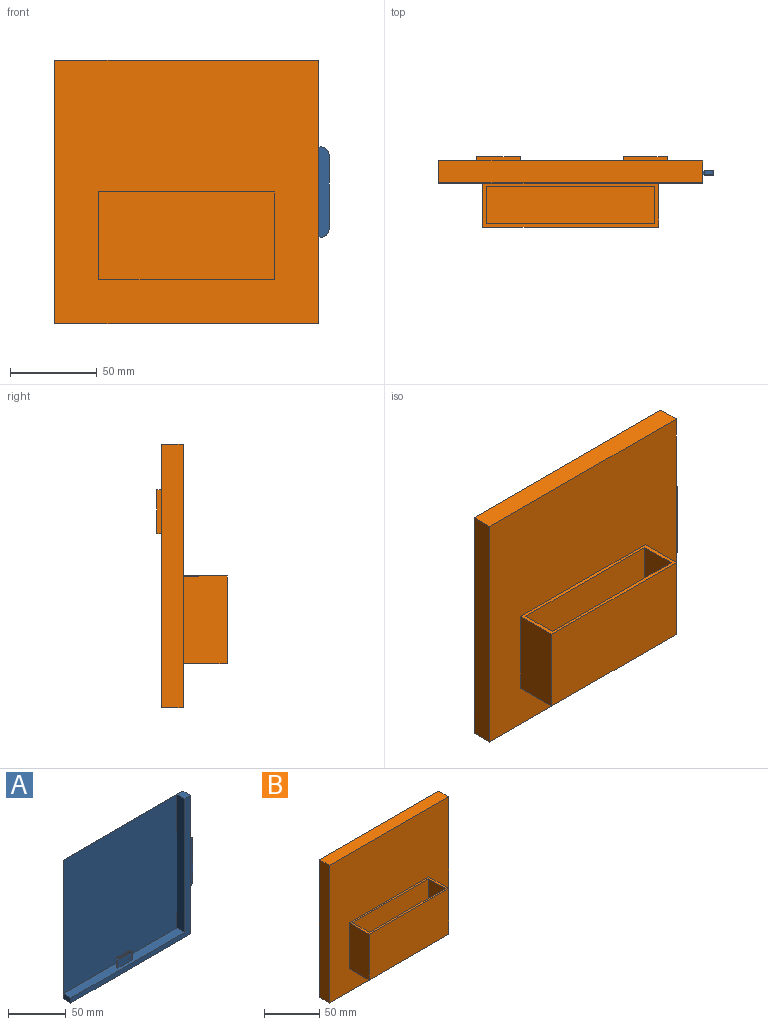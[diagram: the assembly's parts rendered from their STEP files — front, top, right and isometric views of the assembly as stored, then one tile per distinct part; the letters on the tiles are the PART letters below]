
ASSEMBLY  parts=2 mates=1
PART A: 38 faces, bbox 152.1x9.5x146.1 mm
  f0: plane 146.05x146.05mm, normal (0,-1,0), area 1798.6mm2, adj f1,f2,f4,f5,f6,f7
  f1: plane 146.05x9.53mm, normal (-1,0,0), area 88.7mm2, adj f0,f2,f3,f4,f6,f8
  f2: plane 146.05x9.53mm, normal (0,0,-1), area 1391.1mm2, adj f0,f1,f3,f5
  f3: plane 146.05x146.05mm, normal (0,1,0), area 21330.6mm2, adj f1,f2,f4,f5
  f4: plane 146.05x9.53mm, normal (0,0,1), area 109.2mm2, adj f0,f1,f3,f5,f7,f8
  f5: plane 146.05x9.53mm, normal (1,0,0), area 1261.8mm2, adj f0,f2,f3,f4,f31,f32,f33,f34
  f6: plane 138.66x9.25mm, normal (0,0,1), area 1222.6mm2, adj f0,f1,f7,f8,f9,f10,f11,f12
  f7: plane 140.87x9.25mm, normal (-1,0,0), area 1302.4mm2, adj f0,f4,f6,f8
  f8: plane 140.87x138.66mm, normal (0,-1,0), area 19532mm2, adj f1,f4,f6,f7
  f9: plane 8.61x1.47mm, normal (-1,0,0), area 12.6mm2, adj f6,f10,f14,f15
  f10: plane 18.06x8.61mm, normal (0,-1,0), area 155.5mm2, adj f6,f9,f11,f15
  f11: plane 8.61x1.47mm, normal (1,0,0), area 12.6mm2, adj f6,f10,f12,f15
  f12: cylinder r=1.91mm len=8.61mm, axis (0,0,-1), area 25.8mm2, adj f6,f11,f13,f15
  f13: plane 14.25x8.61mm, normal (0,1,0), area 122.7mm2, adj f6,f12,f14,f15
  f14: cylinder r=1.91mm len=8.61mm, axis (0,0,-1), area 25.8mm2, adj f6,f9,f13,f15
  f15: plane 18.06x3.37mm, normal (0,0,1), area 21.9mm2, adj f9,f10,f11,f12,f13,f14,f16,f17
  f16: plane 6.07x2.45mm, normal (1,0,0), area 14.9mm2, adj f15,f17,f24,f25
  f17: plane 15.28x6.07mm, normal (0,1,0), area 92.8mm2, adj f15,f16,f18,f25
  f18: plane 6.07x2.45mm, normal (-1,0,0), area 14.9mm2, adj f15,f17,f24,f25
  f19: cylinder r=0.68mm len=6.07mm, axis (0,0,1), area 25.9mm2, adj f25,f26
  f20: cylinder r=0.68mm len=6.07mm, axis (0,0,1), area 25.8mm2, adj f25,f27
  f21: cylinder r=0.87mm len=6.07mm, axis (0,0,1), area 33.3mm2, adj f25,f28
  f22: cylinder r=0.6mm len=6.07mm, axis (0,0,1), area 22.8mm2, adj f25,f29
  f23: cylinder r=0.59mm len=6.07mm, axis (0,0,1), area 22.7mm2, adj f25,f30
  f24: plane 15.28x6.07mm, normal (0,-1,0), area 92.8mm2, adj f15,f16,f18,f25
  f25: plane 15.28x2.45mm, normal (0,0,1), area 30mm2, adj f16,f17,f18,f19,f20,f21,f22,f23
  f26: plane 1.36x1.36mm, normal (0,0,1), area 1.4mm2, adj f19
  f27: plane 1.35x1.35mm, normal (0,0,1), area 1.4mm2, adj f20
  f28: plane 1.75x1.75mm, normal (0,0,1), area 2.4mm2, adj f21
  f29: plane 1.19x1.19mm, normal (0,0,1), area 1.1mm2, adj f22
  f30: plane 1.19x1.19mm, normal (0,0,1), area 1.1mm2, adj f23
  f31: plane 52.3x6.1mm, normal (0,-1,0), area 307.7mm2, adj f5,f32,f34,f35,f36,f37
  f32: plane 2.47x1.02mm, normal (0,0,-1), area 2.5mm2, adj f5,f31,f33,f36
  f33: plane 52.3x6.1mm, normal (0,1,0), area 307.7mm2, adj f5,f32,f34,f35,f36,f37
  f34: plane 2.47x1.02mm, normal (0,0,1), area 2.5mm2, adj f5,f31,f33,f37
  f35: plane 42.14x2.47mm, normal (1,0,0), area 104.2mm2, adj f31,f33,f36,f37
  f36: cylinder r=5.08mm len=5.08mm, axis (0,-1,0), area 19.7mm2, adj f31,f32,f33,f35
  f37: cylinder r=5.08mm len=5.08mm, axis (0,1,0), area 19.7mm2, adj f31,f33,f34,f35
PART B: 31 faces, bbox 152.4x40.6x152.4 mm
  f0: plane 152.4x152.4mm, normal (0,1,0), area 21935.4mm2, adj f1,f2,f3,f4,f6,f7,f8,f9
  f1: plane 152.4x12.7mm, normal (-1,0,0), area 1935.5mm2, adj f0,f2,f4,f5
  f2: plane 152.4x12.7mm, normal (0,0,-1), area 1935.5mm2, adj f0,f1,f3,f5
  f3: plane 152.4x12.7mm, normal (1,0,0), area 544.4mm2, adj f0,f2,f4,f5,f16,f17,f18,f19
  f4: plane 152.4x12.7mm, normal (0,0,1), area 1935.5mm2, adj f0,f1,f3,f5
  f5: plane 152.4x152.4mm, normal (0,-1,0), area 18064.5mm2, adj f1,f2,f3,f4,f21,f22,f23,f24
  f6: plane 25.4x2.54mm, normal (1,0,0), area 64.5mm2, adj f0,f7,f9,f10
  f7: plane 25.4x2.54mm, normal (0,0,-1), area 64.5mm2, adj f0,f6,f8,f10
  f8: plane 25.4x2.54mm, normal (-1,0,0), area 64.5mm2, adj f0,f7,f9,f10
  f9: plane 25.4x2.54mm, normal (0,0,1), area 64.5mm2, adj f0,f6,f8,f10
  f10: plane 25.4x25.4mm, normal (0,1,0), area 645.2mm2, adj f6,f7,f8,f9
  f11: plane 25.4x2.54mm, normal (1,0,0), area 64.5mm2, adj f0,f12,f14,f15
  f12: plane 25.4x2.54mm, normal (0,0,-1), area 64.5mm2, adj f0,f11,f13,f15
  f13: plane 25.4x2.54mm, normal (-1,0,0), area 64.5mm2, adj f0,f12,f14,f15
  f14: plane 25.4x2.54mm, normal (0,0,1), area 64.5mm2, adj f0,f11,f13,f15
  f15: plane 25.4x25.4mm, normal (0,1,0), area 645.2mm2, adj f11,f12,f13,f14
  f16: plane 146.05x146.05mm, normal (0,1,0), area 21330.6mm2, adj f3,f17,f19,f20
  f17: plane 146.05x9.53mm, normal (0,0,1), area 1391.1mm2, adj f3,f16,f18,f20
  f18: plane 146.05x146.05mm, normal (0,-1,0), area 21330.6mm2, adj f3,f17,f19,f20
  f19: plane 146.05x9.53mm, normal (0,0,-1), area 1391.1mm2, adj f3,f16,f18,f20
  f20: plane 146.05x9.53mm, normal (1,0,0), area 1391.1mm2, adj f16,f17,f18,f19
  f21: plane 50.8x25.4mm, normal (-1,0,0), area 1290.3mm2, adj f5,f22,f24,f25
  f22: plane 101.6x25.4mm, normal (0,0,-1), area 2580.6mm2, adj f5,f21,f23,f25
  f23: plane 50.8x25.4mm, normal (1,0,0), area 1290.3mm2, adj f5,f22,f24,f25
  f24: plane 101.6x25.4mm, normal (0,0,1), area 484.7mm2, adj f5,f21,f23,f25,f26,f27,f28,f29
  f25: plane 101.6x50.8mm, normal (0,-1,0), area 5161.3mm2, adj f21,f22,f23,f24
  f26: plane 46.99x21.57mm, normal (1,0,0), area 1013.5mm2, adj f24,f27,f29,f30
  f27: plane 97.18x46.99mm, normal (0,1,0), area 4566.4mm2, adj f24,f26,f28,f30
  f28: plane 46.99x21.57mm, normal (-1,0,0), area 1013.5mm2, adj f24,f27,f29,f30
  f29: plane 97.18x46.99mm, normal (0,-1,0), area 4566.4mm2, adj f24,f26,f28,f30
  f30: plane 97.18x21.57mm, normal (0,0,1), area 2095.9mm2, adj f26,f27,f28,f29
PLACE A t=(128.55,123.58,22.8)mm
PLACE B t=(128.55,123.73,22.86)mm fixed
MATE slider B.f20 <-> A.f1  axis (1,0,0) through (58.7,130.08,22.86)mm
